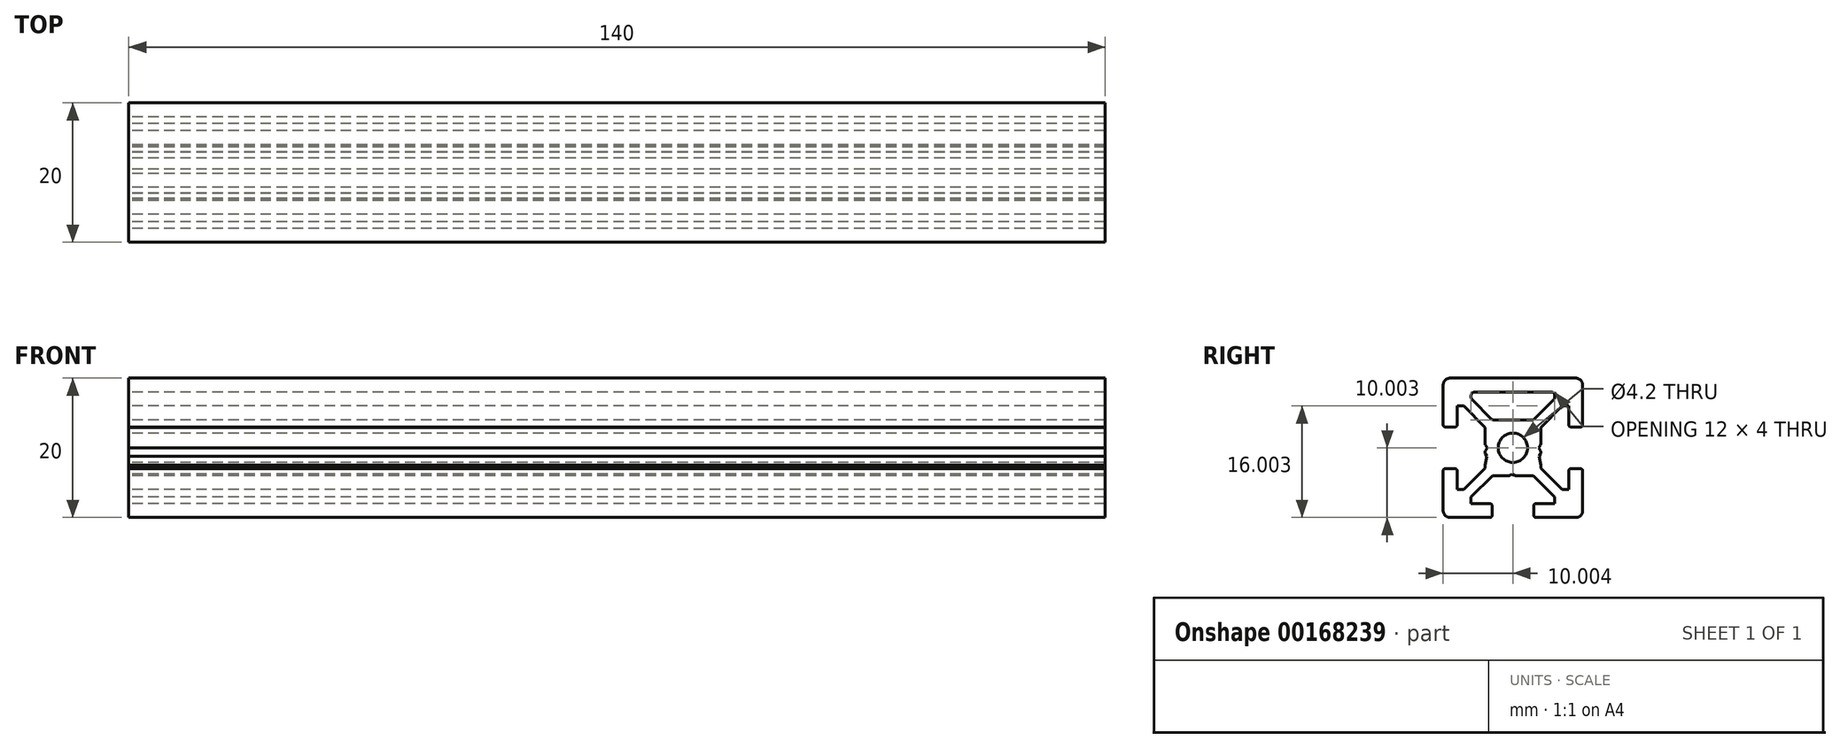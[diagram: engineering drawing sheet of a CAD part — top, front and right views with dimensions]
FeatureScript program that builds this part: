
annotation { "Feature Type Name" : "Feature", "Feature Type Description" : "" }
export const myFeature = defineFeature(function(context is Context, id is Id, definition is map)
    precondition{}
    {
        {
            var Q0;
            Q0=qCreatedBy(makeId("Right.planeOp"),FACE);
            var sketch = newSketch(context, id + "F0", { "sketchPlane" : qUnion([Q0])});
            skLineSegment(sketch, "E0", {"start": v(0.04, 10.07) * mm, "end": v(-8.96, 10.07) * mm});
            skLineSegment(sketch, "E1", {"start": v(-9.96, 9.07) * mm, "end": v(-9.96, 3.37) * mm});
            skLineSegment(sketch, "E2", {"start": v(-3.96, 3.01) * mm, "end": v(-3.96, 0.73) * mm});
            skLineSegment(sketch, "E3", {"start": v(0.04, 4.07) * mm, "end": v(-2.69, 4.07) * mm});
            skLineSegment(sketch, "E4", {"start": v(0.04, 8.07) * mm, "end": v(-5.46, 8.07) * mm});
            skLineSegment(sketch, "E5", {"start": v(-7.96, 6.07) * mm, "end": v(-7.96, 3.37) * mm});
            skLineSegment(sketch, "E6", {"start": v(-8.26, 3.07) * mm, "end": v(-9.66, 3.07) * mm});
            skLineSegment(sketch, "E7", {"start": v(-8.26, -2.93) * mm, "end": v(-9.66, -2.93) * mm});
            skLineSegment(sketch, "E8", {"start": v(-7.02, -5.93) * mm, "end": v(-7.96, -5.93) * mm});
            skLineSegment(sketch, "E9", {"start": v(-7.96, -3.23) * mm, "end": v(-7.96, -5.93) * mm});
            skLineSegment(sketch, "E10", {"start": v(-9.96, -3.23) * mm, "end": v(-9.96, -8.93) * mm});
            skLineSegment(sketch, "E11", {"start": v(-7.02, 6.07) * mm, "end": v(-7.96, 6.07) * mm});
            skLineSegment(sketch, "E12", {"start": v(-3.89, -0.33) * mm, "end": v(-3.66, 0.07) * mm});
            skLineSegment(sketch, "E13", {"start": v(-3.89, 0.48) * mm, "end": v(-3.66, 0.07) * mm});
            skLineSegment(sketch, "E14", {"start": v(-3.96, -2.43) * mm, "end": v(-3.96, -2.87) * mm});
            skLineSegment(sketch, "E15", {"start": v(-3.96, 3.01) * mm, "end": v(-7.02, 6.07) * mm});
            skLineSegment(sketch, "E16", {"start": v(-3.96, -2.87) * mm, "end": v(-7.02, -5.93) * mm});
            skLineSegment(sketch, "E17", {"start": v(-3.96, -2.43) * mm, "end": v(-3.7, -1.15) * mm});
            skArc(sketch, "E18", {"start": v(-3.89, -0.33) * mm, "mid": v(-3.96, -0.58) * mm, "end": v(-3.89, -0.83) * mm});
            skLineSegment(sketch, "E19", {"start": v(-3.89, -0.83) * mm, "end": v(-3.7, -1.15) * mm});
            skArc(sketch, "E20", {"start": v(-3.96, 0.73) * mm, "mid": v(-3.94, 0.6) * mm, "end": v(-3.89, 0.48) * mm});
            skArc(sketch, "E21", {"start": v(-8.26, 3.07) * mm, "mid": v(-8.04, 3.16) * mm, "end": v(-7.96, 3.37) * mm});
            skArc(sketch, "E22", {"start": v(-9.96, 3.37) * mm, "mid": v(-9.87, 3.16) * mm, "end": v(-9.66, 3.07) * mm});
            skArc(sketch, "E23", {"start": v(-7.96, -3.23) * mm, "mid": v(-8.04, -3.01) * mm, "end": v(-8.26, -2.93) * mm});
            skArc(sketch, "E24", {"start": v(-9.66, -2.93) * mm, "mid": v(-9.87, -3.01) * mm, "end": v(-9.96, -3.23) * mm});
            skLineSegment(sketch, "E25", {"start": v(-2.9, -3.93) * mm, "end": v(-0.61, -3.93) * mm});
            skArc(sketch, "E26", {"start": v(-3.26, -9.93) * mm, "mid": v(-3.04, -9.84) * mm, "end": v(-2.96, -9.63) * mm});
            skLineSegment(sketch, "E27", {"start": v(-5.96, -7.93) * mm, "end": v(-3.26, -7.93) * mm});
            skArc(sketch, "E28", {"start": v(-2.96, -8.23) * mm, "mid": v(-3.04, -8.01) * mm, "end": v(-3.26, -7.93) * mm});
            skLineSegment(sketch, "E29", {"start": v(-5.96, -6.99) * mm, "end": v(-5.96, -7.93) * mm});
            skLineSegment(sketch, "E30", {"start": v(-2.96, -8.23) * mm, "end": v(-2.96, -9.63) * mm});
            skLineSegment(sketch, "E31", {"start": v(-0.36, -3.86) * mm, "end": v(-0.06, -3.69) * mm});
            skArc(sketch, "E32", {"start": v(-0.61, -3.93) * mm, "mid": v(-0.48, -3.9) * mm, "end": v(-0.36, -3.86) * mm});
            skLineSegment(sketch, "E33", {"start": v(-2.9, -3.93) * mm, "end": v(-5.96, -6.99) * mm});
            skLineSegment(sketch, "E34", {"start": v(-3.26, -9.93) * mm, "end": v(-8.96, -9.93) * mm});
            skLineSegment(sketch, "E35", {"start": v(-3.04, 4.22) * mm, "end": v(-5.8, 6.99) * mm});
            skLineSegment(sketch, "E36", {"start": v(-5.96, 7.57) * mm, "end": v(-5.96, 7.34) * mm});
            skArc(sketch, "E37", {"start": v(0.04, -2.03) * mm, "mid": v(-2.06, 0.07) * mm, "end": v(0.04, 2.17) * mm});
            skArc(sketch, "E38", {"start": v(-9.96, -8.93) * mm, "mid": v(-9.66, -9.63) * mm, "end": v(-8.96, -9.93) * mm});
            skArc(sketch, "E39", {"start": v(-8.96, 10.07) * mm, "mid": v(-9.66, 9.78) * mm, "end": v(-9.96, 9.07) * mm});
            skArc(sketch, "E40", {"start": v(-5.46, 8.07) * mm, "mid": v(-5.8, 7.93) * mm, "end": v(-5.96, 7.57) * mm});
            skArc(sketch, "E41", {"start": v(-5.96, 7.34) * mm, "mid": v(-5.92, 7.15) * mm, "end": v(-5.8, 6.99) * mm});
            skArc(sketch, "E42", {"start": v(-3.04, 4.22) * mm, "mid": v(-2.88, 4.11) * mm, "end": v(-2.69, 4.07) * mm});
            skArc(sketch, "E43.MirrorCS", {"start": v(8.34, 3.07) * mm, "mid": v(8.13, 3.16) * mm, "end": v(8.04, 3.37) * mm});
            skArc(sketch, "E44.MirrorCS", {"start": v(5.54, 8.07) * mm, "mid": v(5.9, 7.93) * mm, "end": v(6.04, 7.57) * mm});
            skLineSegment(sketch, "E45.MirrorCS", {"start": v(3.98, -0.33) * mm, "end": v(3.74, 0.07) * mm});
            skArc(sketch, "E46.MirrorCS", {"start": v(3.04, -8.23) * mm, "mid": v(3.13, -8.01) * mm, "end": v(3.34, -7.93) * mm});
            skLineSegment(sketch, "E47.MirrorCS", {"start": v(3.98, -0.83) * mm, "end": v(3.8, -1.15) * mm});
            skArc(sketch, "E48.MirrorCS", {"start": v(3.34, -9.93) * mm, "mid": v(3.13, -9.84) * mm, "end": v(3.04, -9.63) * mm});
            skLineSegment(sketch, "E49.MirrorCS", {"start": v(7.1, -5.93) * mm, "end": v(8.04, -5.93) * mm});
            skArc(sketch, "E50.MirrorCS", {"start": v(3.98, -0.33) * mm, "mid": v(4.04, -0.58) * mm, "end": v(3.98, -0.83) * mm});
            skLineSegment(sketch, "E51.MirrorCS", {"start": v(4.04, -2.43) * mm, "end": v(3.8, -1.15) * mm});
            skArc(sketch, "E52.MirrorCS", {"start": v(9.74, -2.93) * mm, "mid": v(9.96, -3.01) * mm, "end": v(10.04, -3.23) * mm});
            skArc(sketch, "E53.MirrorCS", {"start": v(0.7, -3.93) * mm, "mid": v(0.63, -3.92) * mm, "end": v(0.57, -3.91) * mm});
            skLineSegment(sketch, "E54.MirrorCS", {"start": v(6.04, 7.57) * mm, "end": v(6.04, 7.34) * mm});
            skLineSegment(sketch, "E55.MirrorCS", {"start": v(6.04, -6.99) * mm, "end": v(6.04, -7.93) * mm});
            skArc(sketch, "E56.MirrorCS", {"start": v(6.04, 7.34) * mm, "mid": v(6, 7.15) * mm, "end": v(5.9, 6.99) * mm});
            skArc(sketch, "E57.MirrorCS", {"start": v(4.04, 0.73) * mm, "mid": v(4.03, 0.6) * mm, "end": v(3.98, 0.48) * mm});
            skArc(sketch, "E58.MirrorCS", {"start": v(8.04, -3.23) * mm, "mid": v(8.13, -3.01) * mm, "end": v(8.34, -2.93) * mm});
            skArc(sketch, "E59.MirrorCS", {"start": v(10.04, 3.37) * mm, "mid": v(9.96, 3.16) * mm, "end": v(9.74, 3.07) * mm});
            skArc(sketch, "E60.MirrorCS", {"start": v(3.13, 4.22) * mm, "mid": v(2.97, 4.11) * mm, "end": v(2.78, 4.07) * mm});
            skLineSegment(sketch, "E61.MirrorCS", {"start": v(7.1, 6.07) * mm, "end": v(8.04, 6.07) * mm});
            skLineSegment(sketch, "E62.MirrorCS", {"start": v(4.04, -2.43) * mm, "end": v(4.04, -2.87) * mm});
            skLineSegment(sketch, "E63.MirrorCS", {"start": v(3.98, 0.48) * mm, "end": v(3.74, 0.07) * mm});
            skLineSegment(sketch, "E64.MirrorCS", {"start": v(3.04, -8.23) * mm, "end": v(3.04, -9.63) * mm});
            skLineSegment(sketch, "E65.MirrorCS", {"start": v(3.13, 4.22) * mm, "end": v(5.9, 6.99) * mm});
            skLineSegment(sketch, "E66.MirrorCS", {"start": v(10.04, -3.23) * mm, "end": v(10.04, -8.93) * mm});
            skLineSegment(sketch, "E67.MirrorCS", {"start": v(8.04, -3.23) * mm, "end": v(8.04, -5.93) * mm});
            skLineSegment(sketch, "E68.MirrorCS", {"start": v(8.34, -2.93) * mm, "end": v(9.74, -2.93) * mm});
            skLineSegment(sketch, "E69.MirrorCS", {"start": v(8.34, 3.07) * mm, "end": v(9.74, 3.07) * mm});
            skLineSegment(sketch, "E70.MirrorCS", {"start": v(2.98, -3.93) * mm, "end": v(0.7, -3.93) * mm});
            skLineSegment(sketch, "E71.MirrorCS", {"start": v(4.04, 3.01) * mm, "end": v(4.04, 0.73) * mm});
            skLineSegment(sketch, "E72.MirrorCS", {"start": v(4.04, -2.87) * mm, "end": v(7.1, -5.93) * mm});
            skLineSegment(sketch, "E73.MirrorCS", {"start": v(2.98, -3.93) * mm, "end": v(6.04, -6.99) * mm});
            skArc(sketch, "E74.MirrorCS", {"start": v(9.04, 10.07) * mm, "mid": v(9.75, 9.78) * mm, "end": v(10.04, 9.07) * mm});
            skLineSegment(sketch, "E75.MirrorCS", {"start": v(6.04, -7.93) * mm, "end": v(3.34, -7.93) * mm});
            skLineSegment(sketch, "E76.MirrorCS", {"start": v(4.04, 3.01) * mm, "end": v(7.1, 6.07) * mm});
            skArc(sketch, "E77.MirrorCS", {"start": v(10.04, -8.93) * mm, "mid": v(9.75, -9.63) * mm, "end": v(9.04, -9.93) * mm});
            skLineSegment(sketch, "E78.MirrorCS", {"start": v(3.34, -9.93) * mm, "end": v(9.04, -9.93) * mm});
            skLineSegment(sketch, "E79.MirrorCS", {"start": v(8.04, 6.07) * mm, "end": v(8.04, 3.37) * mm});
            skLineSegment(sketch, "E80.MirrorCS", {"start": v(10.04, 9.07) * mm, "end": v(10.04, 3.37) * mm});
            skLineSegment(sketch, "E81.MirrorCS", {"start": v(0.04, 10.07) * mm, "end": v(9.04, 10.07) * mm});
            skLineSegment(sketch, "E82.MirrorCS", {"start": v(0.04, 8.07) * mm, "end": v(5.54, 8.07) * mm});
            skLineSegment(sketch, "E83.MirrorCS", {"start": v(0.04, 4.07) * mm, "end": v(2.78, 4.07) * mm});
            skArc(sketch, "E84.MirrorCS", {"start": v(0.04, -2.03) * mm, "mid": v(2.14, 0.07) * mm, "end": v(0.04, 2.17) * mm});
            skLineSegment(sketch, "E85", {"start": v(0.22, -3.85) * mm, "end": v(-0.06, -3.69) * mm});
            skArc(sketch, "E86", {"start": v(0.22, -3.85) * mm, "mid": v(0.4, -3.92) * mm, "end": v(0.57, -3.91) * mm});
            skSolve(sketch);
        }
        {
            var Q0;
            Q0=qSketchRegion(id+"F0",true);
            extrude(context, id + "F1", {"entities" : qUnion([Q0]), "endBound" : BoundingType.SYMMETRIC, "depth" : 140 * mm});
        }
    });
